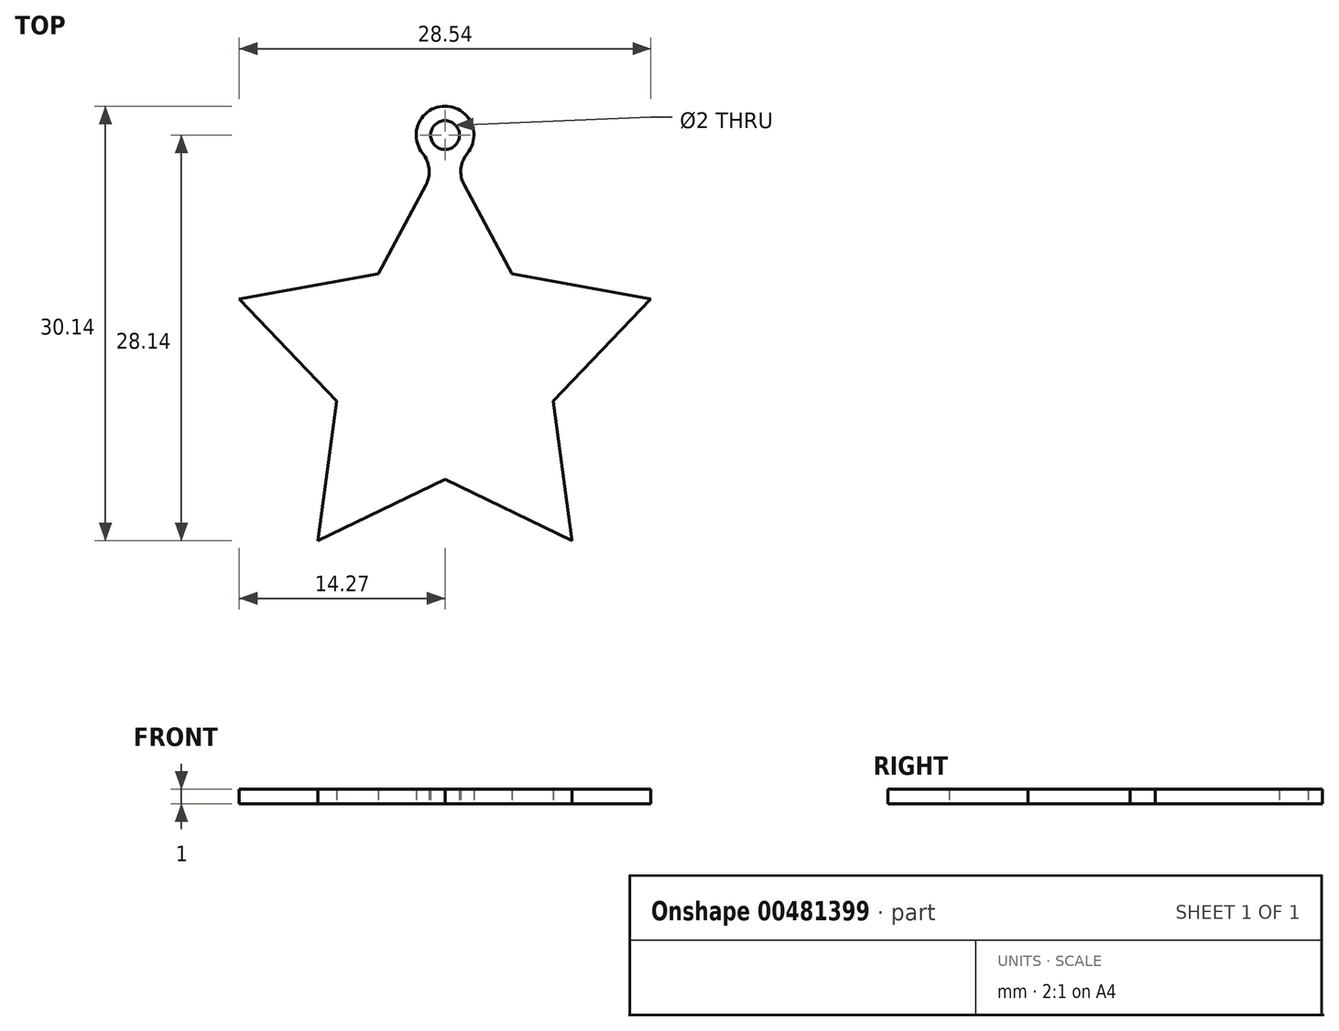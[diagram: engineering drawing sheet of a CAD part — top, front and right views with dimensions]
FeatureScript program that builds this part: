
annotation { "Feature Type Name" : "Feature", "Feature Type Description" : "" }
export const myFeature = defineFeature(function(context is Context, id is Id, definition is map)
    precondition{}
    {
        {
            var Q0;
            Q0=qCreatedBy(makeId("Top.planeOp"),FACE);
            var sketch = newSketch(context, id + "F0", { "sketchPlane" : qUnion([Q0])});
            skCircle(sketch, "E0", {"center": v(0, 0) * mm, "radius": 15 * mm, "construction": true});
            skCircle(sketch, "E1", {"center": v(0, 0) * mm, "radius": 7.89 * mm, "construction": true});
            skLineSegment(sketch, "E2", {"start": v(0, 15) * mm, "end": v(4.64, 6.38) * mm});
            skLineSegment(sketch, "E3", {"start": v(4.64, 6.38) * mm, "end": v(14.27, 4.64) * mm});
            skLineSegment(sketch, "E4", {"start": v(14.27, 4.64) * mm, "end": v(7.5, -2.44) * mm});
            skLineSegment(sketch, "E5", {"start": v(7.5, -2.44) * mm, "end": v(8.82, -12.14) * mm});
            skLineSegment(sketch, "E6", {"start": v(8.82, -12.14) * mm, "end": v(0, -7.89) * mm});
            skLineSegment(sketch, "E7", {"start": v(0, -7.89) * mm, "end": v(-8.82, -12.14) * mm});
            skLineSegment(sketch, "E8", {"start": v(-8.82, -12.14) * mm, "end": v(-7.5, -2.44) * mm});
            skLineSegment(sketch, "E9", {"start": v(-7.5, -2.44) * mm, "end": v(-14.27, 4.64) * mm});
            skLineSegment(sketch, "E10", {"start": v(-14.27, 4.64) * mm, "end": v(-4.64, 6.38) * mm});
            skLineSegment(sketch, "E11", {"start": v(-4.64, 6.38) * mm, "end": v(0, 15) * mm});
            skLineSegment(sketch, "E12", {"start": v(-8.82, -12.14) * mm, "end": v(4.64, 6.38) * mm, "construction": true});
            skLineSegment(sketch, "E13", {"start": v(-14.27, 4.64) * mm, "end": v(7.5, -2.44) * mm, "construction": true});
            skLineSegment(sketch, "E14", {"start": v(-7.5, -2.44) * mm, "end": v(14.27, 4.64) * mm, "construction": true});
            skLineSegment(sketch, "E15", {"start": v(-4.64, 6.38) * mm, "end": v(8.82, -12.14) * mm, "construction": true});
            skCircle(sketch, "E16", {"center": v(0, 16) * mm, "radius": 1 * mm});
            skCircle(sketch, "E17", {"center": v(0, 16) * mm, "radius": 2 * mm});
            skArc(sketch, "E18", {"start": v(1.55, 14.73) * mm, "mid": v(1.1, 13.66) * mm, "end": v(1.33, 12.52) * mm});
            skArc(sketch, "E19", {"start": v(-1.33, 12.52) * mm, "mid": v(-1.1, 13.66) * mm, "end": v(-1.55, 14.73) * mm});
            skLineSegment(sketch, "E20.bottom", {"start": v(-21.47, 22.85) * mm, "end": v(29.65, 22.85) * mm, "construction": true});
            skLineSegment(sketch, "E20.top", {"start": v(-21.47, -17.47) * mm, "end": v(29.65, -17.47) * mm, "construction": true});
            skLineSegment(sketch, "E20.left", {"start": v(-21.47, 22.85) * mm, "end": v(-21.47, -17.47) * mm, "construction": true});
            skLineSegment(sketch, "E20.right", {"start": v(29.65, 22.85) * mm, "end": v(29.65, -17.47) * mm, "construction": true});
            skSolve(sketch);
        }
        {
            var Q0;
            {var subQ5=sQuery(id+"F0.wireOp",EDGE,"E3");Q0=makeQuery(id+"F0.imprint","IMPRINT",FACE,{"disambiguationData":[TD([[makeQuery(id+"F0.imprint","IMPRINT",EDGE,{"derivedFrom":subQ5}),-1.0]])]});}
            var Q1;
            {var subQ0=sQuery(id+"F0.wireOp",EDGE,"E18");Q1=makeQuery(id+"F0.imprint","IMPRINT",FACE,{"disambiguationData":[TD([[makeQuery(id+"F0.imprint","IMPRINT",EDGE,{"derivedFrom":subQ0}),-1.0]])]});}
            var Q2;
            {var subQ1=sQuery(id+"F0.wireOp",EDGE,"E2");var subQ3=sQuery(id+"F0.wireOp",EDGE,"E17");var subQ4=makeQuery(id+"F0.imprint","INTERSECT",VERTEX,{"derivedFrom":[subQ1,subQ3]});Q2=makeQuery(id+"F0.imprint","IMPRINT",FACE,{"disambiguationData":[TD([[makeQuery(id+"F0.imprint","IMPRINT",EDGE,{"disambiguationData":[TD([[subQ4,1.0]])],"derivedFrom":subQ3}),1.0]])]});}
            var Q3;
            {var subQ0=sQuery(id+"F0.wireOp",EDGE,"E19");Q3=makeQuery(id+"F0.imprint","IMPRINT",FACE,{"disambiguationData":[TD([[makeQuery(id+"F0.imprint","IMPRINT",EDGE,{"derivedFrom":subQ0}),-1.0]])]});}
            var Q4;
            {var subQ0=sQuery(id+"F0.wireOp",EDGE,"E16");Q4=makeQuery(id+"F0.imprint","IMPRINT",FACE,{"disambiguationData":[TD([[makeQuery(id+"F0.imprint","IMPRINT",EDGE,{"derivedFrom":subQ0}),-1.0]])]});}
            extrude(context, id + "F1", {"entities" : qUnion([Q0, Q1, Q2, Q3, Q4]), "depth" : 1 * mm});
        }
    });
